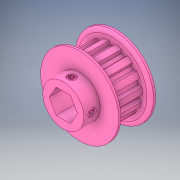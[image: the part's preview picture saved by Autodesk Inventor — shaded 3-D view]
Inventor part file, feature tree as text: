
AUTODESK INVENTOR PART (.ipt)
format: ipt  version: 2017 SP1 (Build 210196100, 196)  size: 244,736 bytes
history: native  units: in
note: dims shown in document units (in); Inventor stores cm internally (conversion verified against a paired STEP export)
features: extrude x1, sketch x1, pattern_circular x1
ambient origin geometry x8: Origin, YZ Plane, XZ Plane, XY Plane, X Axis, Y Axis, Z Axis, Center Point
bodies: Solid1 (feature_tree)
feature tree (3):
  extrude  "Extrusion1"  Depth=1.0in TaperAngle=0.0deg
  sketch  "Sketch1"  dims[d0=0.375in d1=1.0in d2=0.0in]
  pattern_circular  "CirPattern2"
